# Revit family: RA-N_Angle_DN25_RFA
name_source: partatom
category: Pipe Accessories
units: mm (PartAtom-declared; Revit-internal decimal feet)

## family parameters
Always vertical = Yes
Cut with Voids When Loaded = No
OmniClass Number = 23.65.55.14.17
OmniClass Title = Adjusting/Controlling Valves for Liquid Services
Part Type = Valve - Breaks Into
Round Connector Dimension = Use Diameter
Shared = No
Work Plane-Based = No

## types (1)
- RA-N_Angle_DN25_Internal_013G0037
    Connection = Internal Thread
    D = 25 mm  [stored 0.082021 ft]
    DB4 = 28 mm  [stored 0.0918635 ft]
    Description = Thermostatic Radiator Valve
    H = 52 mm
    H1 = 8 mm  [stored 0.0262467 ft]
    H2 = 4 mm  [stored 0.0131234 ft]
    H3 = 9 mm  [stored 0.0295276 ft]
    HH = 34 mm
    HH1 = 15 mm  [stored 0.0492126 ft]
    HH2 = 8 mm  [stored 0.0262467 ft]
    HH3 = 4 mm  [stored 0.0131234 ft]
    IfcExportAs = IfcValveType
    IfcExportType = RA-N
    Kvs = 1.4 m³/h
    L = 76 mm  [stored 0.249344 ft]
    L1 = 25 mm  [stored 0.082021 ft]
    L2 = 6 mm  [stored 0.019685 ft]
    L4 = 19 mm  [stored 0.062336 ft]
    LOD 200 = No
    LOD 350 = Yes
    L_1 = 31 mm
    L_Thread1 = 20 mm  [stored 0.0656168 ft]
    L_Thread2 = 23 mm
    Manufacturer = Danfoss
    Max Differential Pressure = 0.6 bar
    Max Medium Temperature = 120 ˚C
    Max Operating Pressure = 10 bar
    Model = 013G0037
    Model Type = RA-N_Angle_DN25_Internal
    RB1 = 16 mm  [stored 0.0524934 ft]
    RB2 = 20 mm  [stored 0.0656168 ft]
    RB3 = 13 mm  [stored 0.0426509 ft]
    RV1 = 14 mm  [stored 0.0459318 ft]
    RV2 = 19 mm  [stored 0.062336 ft]
    RV3 = 19 mm  [stored 0.062336 ft]
    RV4 = 17 mm
    URL = https://store.danfoss.com
    Valve Body Material = Danfoss Nickel Plated Brass
    Weight = 0.60 kg

note: [stored X ft] marks values corroborated as IEEE doubles in the binary element streams (Revit-internal decimal feet)

## geometry (parser evidence)
native form markers: Sweep x2
no freeform markers — native parametric forms only
